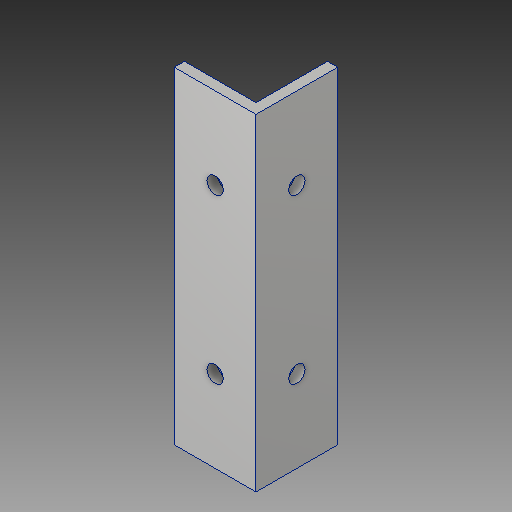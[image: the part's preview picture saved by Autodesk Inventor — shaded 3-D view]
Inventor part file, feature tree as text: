
AUTODESK INVENTOR PART (.ipt)
format: ipt  version: 2018 (Build 220112000, 112)  size: 124,416 bytes
history: native  units: in
note: dims shown in document units (in); Inventor stores cm internally (conversion verified against a paired STEP export)
features: extrude x3, sketch x3
ambient origin geometry x8: Origin, YZ Plane, XZ Plane, XY Plane, X Axis, Y Axis, Z Axis, Center Point
bodies: Solid1 (feature_tree)
feature tree (6):
  extrude  "Extrusion1"  Depth=0.125in
  extrude  "Extrusion2"  Depth=0.125in
  extrude  "Extrusion3"  Depth=1.0in
  sketch  "Sketch1"  dims[d0=1.0in d1=0.125in]
  sketch  "Sketch2"  dims[d2=1.0in d3=0.125in]
  sketch  "Sketch3"  dims[d4=4.0in d5=0.0in d6=0.5in d7=1.0in d8=1.0in d9=0.2in d10=1.0in d11=0.0in d12=1.0in d13=1.0in d14=0.2in d15=1.0in d16=0.0in]
